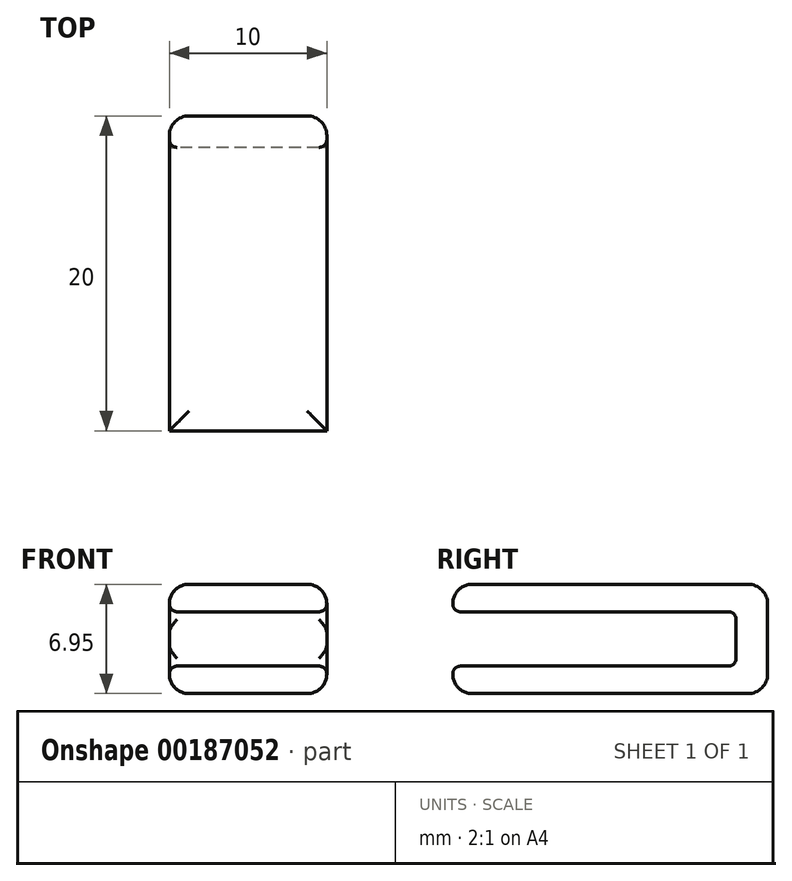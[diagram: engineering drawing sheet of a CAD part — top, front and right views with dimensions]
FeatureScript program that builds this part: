
annotation { "Feature Type Name" : "Feature", "Feature Type Description" : "" }
export const myFeature = defineFeature(function(context is Context, id is Id, definition is map)
    precondition{}
    {
        {
            var Q0;
            Q0=qCreatedBy(makeId("Top.planeOp"),FACE);
            var sketch = newSketch(context, id + "F0", { "sketchPlane" : qUnion([Q0])});
            skLineSegment(sketch, "E0", {"start": v(0, 9) * mm, "end": v(0, -9) * mm, "construction": true});
            skLineSegment(sketch, "E1.bottom", {"start": v(5, 9) * mm, "end": v(-5, 9) * mm});
            skLineSegment(sketch, "E1.top", {"start": v(5, -9) * mm, "end": v(-5, -9) * mm});
            skLineSegment(sketch, "E1.left", {"start": v(5, 9) * mm, "end": v(5, -9) * mm});
            skLineSegment(sketch, "E1.right", {"start": v(-5, 9) * mm, "end": v(-5, -9) * mm});
            skPoint(sketch, "E1.middle", {"position": v(0, 0) * mm});
            skSolve(sketch);
        }
        {
            var Q0;
            Q0 = qSketchRegion(id + "F0", true);
            extrude(context, id + "F1", {"entities" : qUnion([Q0]), "depth" : 1.75 * mm});
        }
        {
            var Q0;
            Q0=makeQuery(id+"F1.opExtrude","SWEPT_FACE",FACE,{"disambiguationData":[OSD([sQuery(id+"F0.wireOp",EDGE,"E1.bottom")])]});
            var sketch = newSketch(context, id + "F2", { "sketchPlane" : qUnion([Q0])});
            skLineSegment(sketch, "E2.bottom", {"start": v(-5, 0) * mm, "end": v(5, 0) * mm});
            skLineSegment(sketch, "E2.top", {"start": v(-5, -5.2) * mm, "end": v(5, -5.2) * mm});
            skLineSegment(sketch, "E2.left", {"start": v(-5, 0) * mm, "end": v(-5, -5.2) * mm});
            skLineSegment(sketch, "E2.right", {"start": v(5, 0) * mm, "end": v(5, -5.2) * mm});
            skLineSegment(sketch, "E3.bottom", {"start": v(-5, 1.75) * mm, "end": v(5, 1.75) * mm});
            skLineSegment(sketch, "E3.left", {"start": v(-5, 1.75) * mm, "end": v(-5, 0) * mm});
            skLineSegment(sketch, "E3.right", {"start": v(5, 1.75) * mm, "end": v(5, 0) * mm});
            skSolve(sketch);
        }
        {
            var Q0;
            Q0 = qSketchRegion(id + "F2", true);
            extrude(context, id + "F3", {"entities" : qUnion([Q0]), "operationType" : NewBodyOperationType.ADD, "depth" : 2 * mm});
        }
        {
            var Q0;
            Q0=makeQuery(id+"F3.boolean.opBoolean","MERGE",FACE,{"derivedFrom":[makeQuery(id+"F1.opExtrude","SWEPT_FACE",FACE,{"disambiguationData":[OSD([sQuery(id+"F0.wireOp",EDGE,"E1.left")])]}),makeQuery(id+"F3.opExtrude","SWEPT_FACE",FACE,{"disambiguationData":[OSD([sQuery(id+"F2.wireOp",EDGE,"E2.left"),sQuery(id+"F2.wireOp",EDGE,"E3.left")])]})]});
            var sketch = newSketch(context, id + "F4", { "sketchPlane" : qUnion([Q0])});
            skLineSegment(sketch, "E4", {"start": v(11, -1.73) * mm, "end": v(1.92, -1.73) * mm, "construction": true});
            skPoint(sketch, "E4.endSnap0", {"position": v(11, -1.73) * mm});
            skSolve(sketch);
        }
        {
            var Q0;
            Q0=makeQuery(id+"F3.boolean.opBoolean","MERGE",FACE,{"derivedFrom":[makeQuery(id+"F1.opExtrude","SWEPT_FACE",FACE,{"disambiguationData":[OSD([sQuery(id+"F0.wireOp",EDGE,"E1.right")])]}),makeQuery(id+"F3.opExtrude","SWEPT_FACE",FACE,{"disambiguationData":[OSD([sQuery(id+"F2.wireOp",EDGE,"E2.right"),sQuery(id+"F2.wireOp",EDGE,"E3.right")])]})]});
            var sketch = newSketch(context, id + "F5", { "sketchPlane" : qUnion([Q0])});
            skLineSegment(sketch, "E5", {"start": v(-11, -1.73) * mm, "end": v(-1.28, -1.72) * mm, "construction": true});
            skSolve(sketch);
        }
        {
            var Q0;
            Q0=sQuery(id+"F5.wireOp",VERTEX,"E5.end");
            var Q1;
            Q1=sQuery(id+"F4.wireOp",VERTEX,"E4.end");
            var Q2;
            Q2=sQuery(id+"F5.wireOp",VERTEX,"E5.start");
            cPlane(context, id + "F6", {"entities" : qUnion([Q0, Q1, Q2]), "cplaneType" : CPlaneType.THREE_POINT, "offset" : 0 * mm, "width" : 150 * mm, "height" : 150 * mm});
        }
        {
            var Q0;
            Q0=makeQuery(id+"F1.opExtrude","SWEPT_BODY",BODY,{"disambiguationData":[OSD([sQuery(id+"F0.wireOp",EDGE,"E1.bottom"),sQuery(id+"F0.wireOp",EDGE,"E1.top"),sQuery(id+"F0.wireOp",EDGE,"E1.left"),sQuery(id+"F0.wireOp",EDGE,"E1.right")])]});
            var Q1;
            Q1=qCreatedBy(id+"F6.planeOp",FACE);
            mirror(context, id + "F7", {"operationType" : NewBodyOperationType.ADD, "entities" : qUnion([Q0]), "mirrorPlane" : qUnion([Q1])});
        }
        {
            var Q0;
            Q0=makeQuery(id+"F1.opExtrude","CAP_EDGE",EDGE,{"disambiguationData":[OSD([sQuery(id+"F0.wireOp",EDGE,"E1.bottom")])],"isStart":true});
            var Q1;
            Q1=makeQuery(id+"F7.opPattern","COPY",EDGE,{"derivedFrom":makeQuery(id+"F1.opExtrude","CAP_EDGE",EDGE,{"disambiguationData":[OSD([sQuery(id+"F0.wireOp",EDGE,"E1.bottom")])],"isStart":true}),"instanceName":"1"});
            var Q2;
            Q2=makeQuery(id+"F7.opPattern","COPY",FACE,{"derivedFrom":makeQuery(id+"F1.opExtrude","CAP_FACE",FACE,{"disambiguationData":[OSD([sQuery(id+"F0.wireOp",EDGE,"E1.bottom"),sQuery(id+"F0.wireOp",EDGE,"E1.top"),sQuery(id+"F0.wireOp",EDGE,"E1.left"),sQuery(id+"F0.wireOp",EDGE,"E1.right")])],"isStart":true}),"instanceName":"1"});
            var Q3;
            Q3=makeQuery(id+"F1.opExtrude","CAP_FACE",FACE,{"disambiguationData":[OSD([sQuery(id+"F0.wireOp",EDGE,"E1.bottom"),sQuery(id+"F0.wireOp",EDGE,"E1.top"),sQuery(id+"F0.wireOp",EDGE,"E1.left"),sQuery(id+"F0.wireOp",EDGE,"E1.right")])],"isStart":true});
            fillet(context, id + "F8", {"entities" : qUnion([Q0, Q1, Q2, Q3]), "radius" : .5 * mm, "tangentPropagation" : true, "allowEdgeOverflow" : false});
        }
        {
            var Q0;
            Q0=makeQuery(id+"F3.opExtrude","CAP_FACE",FACE,{"disambiguationData":[OSD([sQuery(id+"F2.wireOp",EDGE,"E2.top"),sQuery(id+"F2.wireOp",EDGE,"E2.left"),sQuery(id+"F2.wireOp",EDGE,"E2.right"),sQuery(id+"F2.wireOp",EDGE,"E3.bottom"),sQuery(id+"F2.wireOp",EDGE,"E3.left"),sQuery(id+"F2.wireOp",EDGE,"E3.right")])],"isStart":false});
            var Q1;
            Q1=makeQuery(id+"F3.boolean.opBoolean","MERGE",FACE,{"derivedFrom":[makeQuery(id+"F1.opExtrude","CAP_FACE",FACE,{"disambiguationData":[OSD([sQuery(id+"F0.wireOp",EDGE,"E1.bottom"),sQuery(id+"F0.wireOp",EDGE,"E1.top"),sQuery(id+"F0.wireOp",EDGE,"E1.left"),sQuery(id+"F0.wireOp",EDGE,"E1.right")])],"isStart":false}),makeQuery(id+"F3.opExtrude","SWEPT_FACE",FACE,{"disambiguationData":[OSD([sQuery(id+"F2.wireOp",EDGE,"E3.bottom")])]})]});
            var Q2;
            Q2=makeQuery(id+"F7.boolean.opBoolean","MERGE",FACE,{"derivedFrom":[makeQuery(id+"F3.opExtrude","SWEPT_FACE",FACE,{"disambiguationData":[OSD([sQuery(id+"F2.wireOp",EDGE,"E2.top")])]}),makeQuery(id+"F7.opPattern","COPY",FACE,{"derivedFrom":makeQuery(id+"F3.boolean.opBoolean","MERGE",FACE,{"derivedFrom":[makeQuery(id+"F1.opExtrude","CAP_FACE",FACE,{"disambiguationData":[OSD([sQuery(id+"F0.wireOp",EDGE,"E1.bottom"),sQuery(id+"F0.wireOp",EDGE,"E1.top"),sQuery(id+"F0.wireOp",EDGE,"E1.left"),sQuery(id+"F0.wireOp",EDGE,"E1.right")])],"isStart":false}),makeQuery(id+"F3.opExtrude","SWEPT_FACE",FACE,{"disambiguationData":[OSD([sQuery(id+"F2.wireOp",EDGE,"E3.bottom")])]})]}),"instanceName":"1"})]});
            fillet(context, id + "F9", {"entities" : qUnion([Q0, Q1, Q2]), "radius" : 1.25 * mm, "tangentPropagation" : true, "allowEdgeOverflow" : false});
        }
    });
